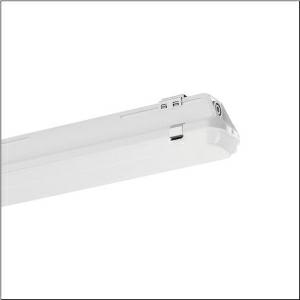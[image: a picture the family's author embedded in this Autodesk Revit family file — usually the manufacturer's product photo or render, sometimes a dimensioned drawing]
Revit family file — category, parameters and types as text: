
# Revit family: monsun_r__12_51fp10ep430h_ed5a
name_source: partatom
category: Lighting Fixtures
units: mm (PartAtom-declared; Revit-internal decimal feet)

## family parameters
Cut with Voids When Loaded = No
Host = Face
Light Source = No
Part Type = Normal
Room Calculation Point = No
Round Connector Dimension = Use Diameter
Shared = No

## types (1)
- --- (1 x LED, 3840 lm, 22.3 W, 4000K)
    Apparent Load = 22 VA
    CIE Flux Codes = 47 77 93 94 100
    Color Rendering = 80
    Color Temperature = 4000K
    Default Elevation = 1800 mm
    Description = Monsun® 12, damp-proof luminaire, chain hanger, primary optical cover: enclosure, of PMMA, light emission: direct distribution, primary light characteristic: symmetric, installation type: suspended mounting, surface-mounted, horizontal mounting, vertical mounting, LED rated luminous flux: 3.840 lm, light colour: 840, colour temperature: 4000K, control gear: ECG DALI, with terminal, 5-pole, max. 2.5mm², mains connection: 220..240V, AC, 50/60Hz, rated input power: 22W, luminaire housing, of glass-fibre reinforced polyester, uncoated, bright grey, length: 1.590 mm, width: 90 mm, height: 88mm, clip for enclosure, of stainless steel (V2A), ceiling mounting element, of stainless steel (V2A), chain hanger, of stainless steel (V2A), protection rating (complete): IP66, insulation class (complete): insulation class I (protective earthing), certification: CE, ENEC, VDE, protection symbol: D, impact resistance: IK04, permissible ambient temperature for indoor applications: -25..+40°C, standard: EN 50419, EN 60598-2-1, no direct snow, no direct sun, no direct rain, for indoor or canopied outdoor use, corresponds to IFS (International Featured Standards) requirements for safety and quality in the food industry, for animal farming (ammonia tested): for use in cowhouse, pig house, horse-stables... (not for use in poultry stables), AT max for animal farming = 40°C, packaging unit: 1 piece
    Height = 89 mm
    Lamp = 1 x LED
    Lamp Light Flux = 3840 lm
    Lamp Power = 22.3 W
    Lamp count = 1
    Length = 1590 mm
    Luminous efficacy = 172 lm/W
    Manufacturer = Siteco
    ModVariant = No
    Model = 51FP10EP430H
    Mounting Place = Ceiling
    Mounting Type = Pendant
    Number of Poles = 1
    OnlyDefault = Yes
    Power Factor = 1
    Product Name = Monsun® 12
    Product group = damp-proof luminaire | ceiling pendant
    ProductGroupID = 908
    Protection Class = Protection class I
    Protection Degree = IP 66
    RLX_Detail_Level = 1
    RlxData = <blob elided: 91893 chars, md5=06efbcfe>
    Socket = socket
    Standby Power = 0 W
    System Light Flux = 3840 lm
    System Power = 22 W
    Type Comments = factory setting: luminous flux: 100 % | dim-lin: 254 | 145 mA
    Type Image = l_1004748.jpg
    URL = http://relux.com
    VarID = @adj_136297
    Voltage = 0 V
    Weight = 0.00 kg
    Width = 90 mm

## geometry (parser evidence)
native form markers: Blend x4, Sweep x13
no freeform markers — native parametric forms only
